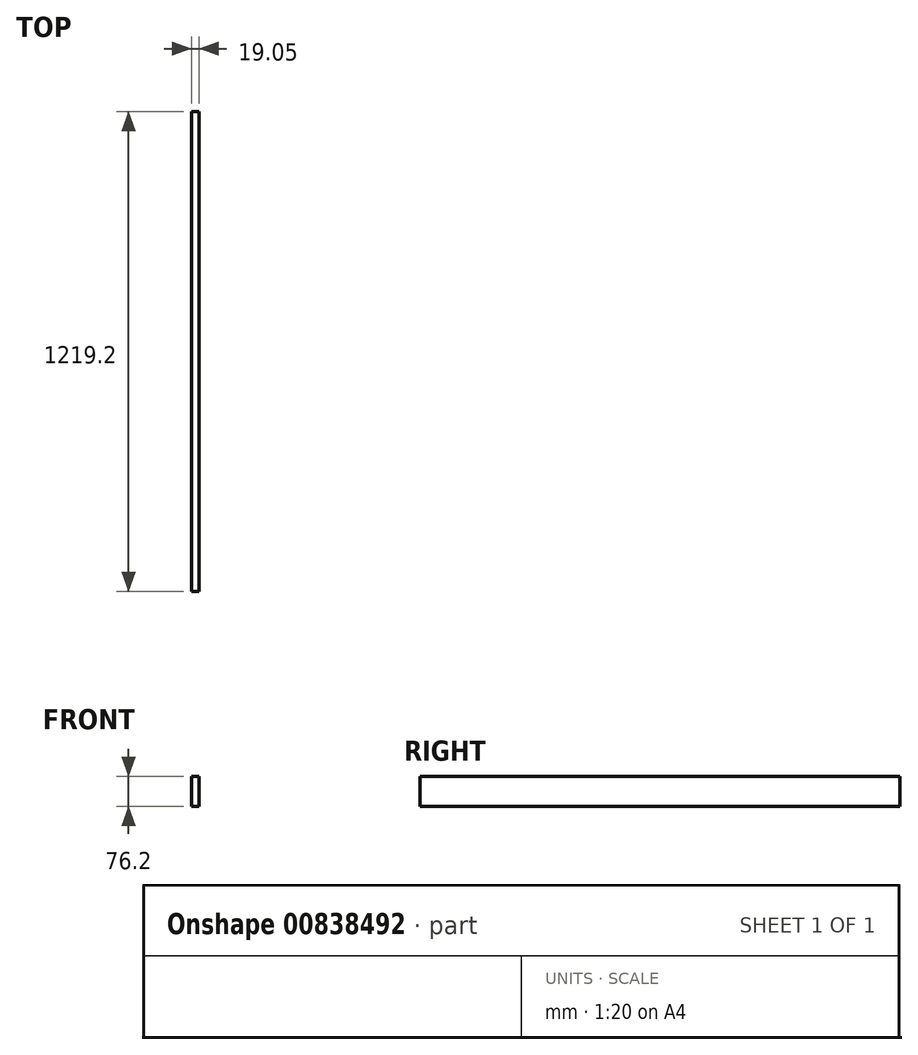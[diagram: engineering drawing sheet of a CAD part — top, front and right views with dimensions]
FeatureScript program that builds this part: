
annotation { "Feature Type Name" : "Feature", "Feature Type Description" : "" }
export const myFeature = defineFeature(function(context is Context, id is Id, definition is map)
    precondition{}
    {
        {
            var Q0;
            Q0=qCreatedBy(makeId("Right.planeOp"),FACE);
            var sketch = newSketch(context, id + "F0", { "sketchPlane" : qUnion([Q0])});
            skLineSegment(sketch, "E0.bottom", {"start": v(-609.6, -38.1) * mm, "end": v(609.6, -38.1) * mm});
            skLineSegment(sketch, "E0.top", {"start": v(-609.6, 38.1) * mm, "end": v(609.6, 38.1) * mm});
            skLineSegment(sketch, "E0.left", {"start": v(-609.6, -38.1) * mm, "end": v(-609.6, 38.1) * mm});
            skLineSegment(sketch, "E0.right", {"start": v(609.6, -38.1) * mm, "end": v(609.6, 38.1) * mm});
            skPoint(sketch, "E0.middle", {"position": v(0, 0) * mm});
            skSolve(sketch);
        }
        {
            var Q0;
            Q0 = qSketchRegion(id + "F0", true);
            extrude(context, id + "F1", {"entities" : qUnion([Q0]), "depth" : 19.05 * mm, "offsetDistance" : 25.4 * mm});
        }
    });
